# Revit family: Data_Device-Network-Leviton-Hinged-Wall_Mount-Bracket
name_source: partatom
category: Data Devices
units: mm (PartAtom-declared; Revit-internal decimal feet)

## family parameters
Classification Number = 23.85.50.17
Cut with Voids When Loaded = No
Host = Face
Maintain Annotation Orientation = Yes
Part Type = Normal
Room Calculation Point = No
Round Connector Dimension = Use Diameter
Shared = Yes

## types (1)
- Hinged wall mount standoff bracket, 2 rack units
    Assembly Code = D5030600
    Bracket Material = Steel - Leviton - Powdercoat - Black
    Date Last Modified = October 06, 2023
    Default Elevation = 24 "
    Depth = 6 "
    Description = Hinged wall mount standoff bracket, 2 rack units
    Equipment Abbreviation = WMB
    Family Version = 1.0.0
    Height = 5.25 "
    Manufacturer = Leviton
    Minimum Order Quantity = 0
    Model Disclaimer = http://www.leviton.com
    Part Description = Hinged wall mount standoff bracket, 2 rack units
    Product Documentation Link = https://www.leviton.com
    Quantity per Package = 0
    URL = http://www.leviton.com
    Width = 19 "
    z Leviton Type = 1

## geometry (parser evidence)
native form markers: Blend x6, Sweep x4
no freeform markers — native parametric forms only
